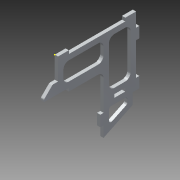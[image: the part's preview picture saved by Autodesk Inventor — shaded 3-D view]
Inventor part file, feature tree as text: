
AUTODESK INVENTOR PART (.ipt)
format: ipt  version: 2015 (Build 190159000, 159)  size: 211,456 bytes
history: native  units: mm
features: sketch x2, extrude x1
ambient origin geometry x8: Origin, YZ Plane, XZ Plane, XY Plane, X Axis, Y Axis, Z Axis, Center Point
bodies: Body1 (feature_tree)
feature tree (3):
  sketch  "Sketch1"  dims[d4=10.0mm d5=52.0mm]
  extrude  "Extrusion5"  Depth=52.0mm
  sketch  "Sketch2"  dims[d6=10.0mm d8=10.0mm d11=3.0mm d15=3.0mm d29=10.0mm d33=5.0mm d36=5.0mm d40=5.0mm d46=30.0mm d47=3.0mm d48=10.0mm d50=3.0mm d53=42.0mm d55=10.0mm d57=3.0mm d59=5.0mm d60=5.0mm d61=5.0mm d62=10.0mm d63=3.0mm d64=10.0mm d67=53.0mm d68=27.0mm d69=5.0mm d75=90.0deg d76=90.0deg d77=90.0deg d78=3.0mm d79=90.0deg d80=6.0mm d81=30.000027mm d82=27.0mm d83=10.0mm d84=10.0mm d85=3.0mm d86=3.0mm d87=30.0mm d90=5.0mm d91=13.0mm d92=33.0mm d95=2.0mm d97=5.0mm d98=5.0mm d99=5.0mm d100=5.0mm d101=2.0mm d102=3.0mm d103=0.0mm d104=5.0mm d105=5.0mm d106=8.0mm d107=33.0mm d108=23.0mm d109=3.0mm d110=2.0mm d111=10.0mm]
